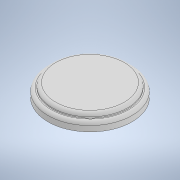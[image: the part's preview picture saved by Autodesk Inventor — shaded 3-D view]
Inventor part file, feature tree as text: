
AUTODESK INVENTOR PART (.ipt)
format: ipt  version: 2022 (Build 260153000, 153)  size: 132,608 bytes
history: native  units: mm
features: revolve x1, fillet x1, sketch x1
ambient origin geometry x8: Origin, YZ Plane, XZ Plane, XY Plane, X Axis, Y Axis, Z Axis, Center Point
bodies: Solid1 (feature_tree)
feature tree (3):
  revolve  "Revolution1"  [1 undecoded]
  fillet  "Fillet1"  Radius=1.0mm
  sketch  "Sketch1"  dims[d0=9.525mm d1=2.0mm d2=1.0mm d3=1.0mm d4=90.0deg d5=0.75mm]
note: 1 required parameter value undecoded (feature->parameter linkage not recoverable at this tier; creation-order binding heuristic only, values carry confidence <= 0.55)
